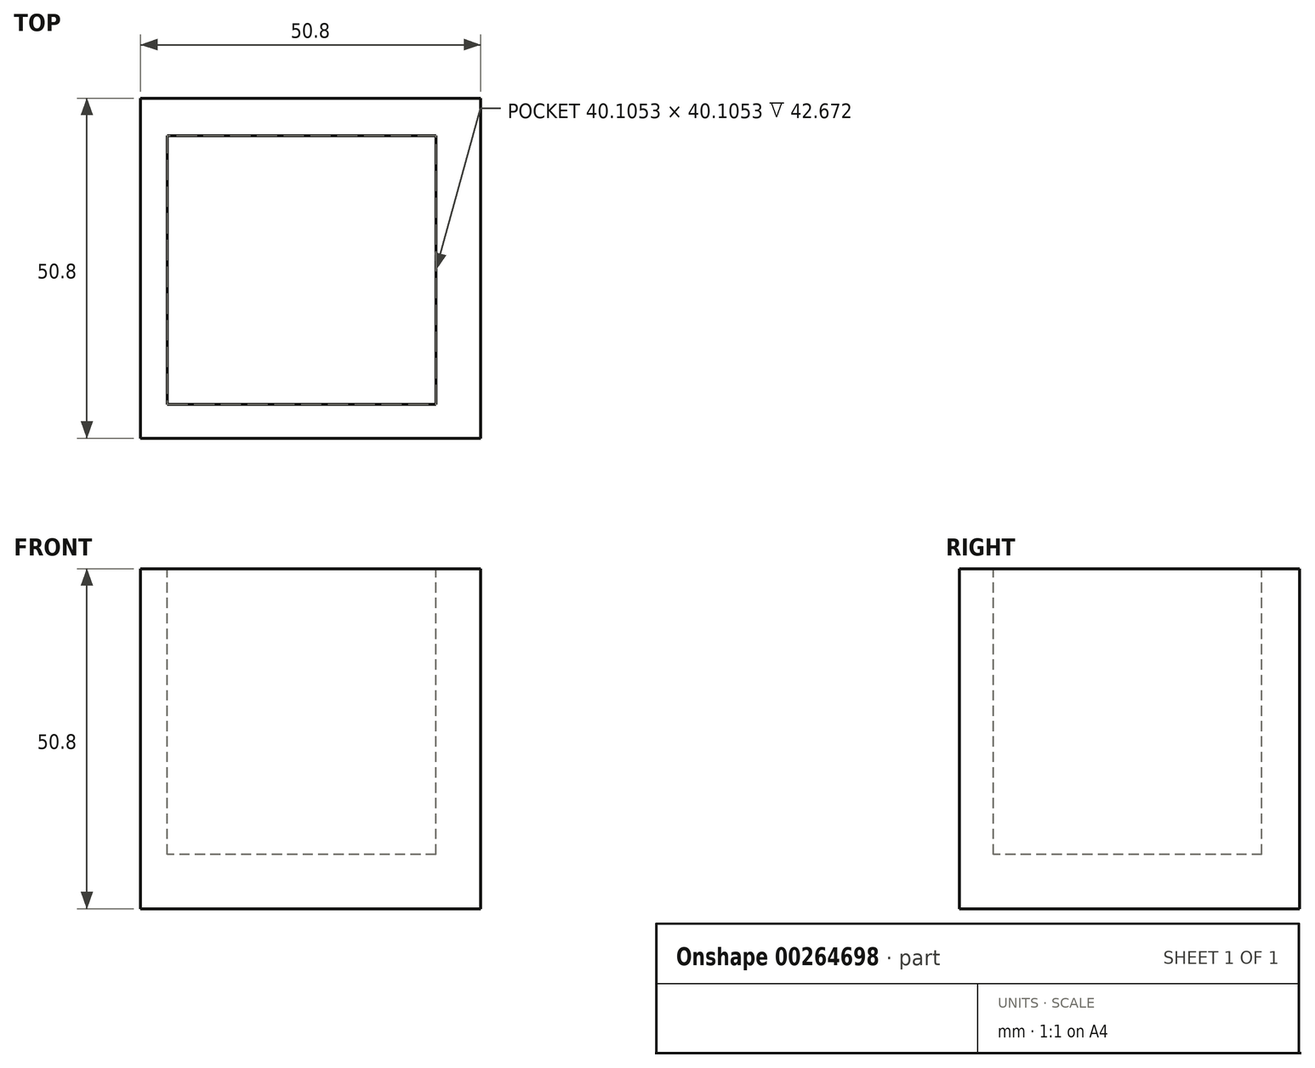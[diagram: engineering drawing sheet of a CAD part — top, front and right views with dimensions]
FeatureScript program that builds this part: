
annotation { "Feature Type Name" : "Feature", "Feature Type Description" : "" }
export const myFeature = defineFeature(function(context is Context, id is Id, definition is map)
    precondition{}
    {
        {
            var Q0;
            Q0=qCreatedBy(makeId("Front.planeOp"),FACE);
            var sketch = newSketch(context, id + "F0", { "sketchPlane" : qUnion([Q0])});
            skLineSegment(sketch, "E0.bottom", {"start": v(0, 0) * mm, "end": v(50.8, 0) * mm});
            skLineSegment(sketch, "E0.top", {"start": v(0, 50.8) * mm, "end": v(50.8, 50.8) * mm});
            skLineSegment(sketch, "E0.left", {"start": v(0, 0) * mm, "end": v(0, 50.8) * mm});
            skLineSegment(sketch, "E0.right", {"start": v(50.8, 0) * mm, "end": v(50.8, 50.8) * mm});
            skSolve(sketch);
        }
        {
            var Q0;
            Q0 = qSketchRegion(id + "F0", true);
            extrude(context, id + "F1", {"entities" : qUnion([Q0]), "depth" : 50.8 * mm});
        }
        {
            var Q0;
            Q0=makeQuery(id+"F1.opExtrude","SWEPT_FACE",FACE,{"disambiguationData":[OSD([sQuery(id+"F0.wireOp",EDGE,"E0.top")])]});
            var sketch = newSketch(context, id + "F2", { "sketchPlane" : qUnion([Q0])});
            skLineSegment(sketch, "E1.bottom", {"start": v(44.12, -5.61) * mm, "end": v(4.01, -5.61) * mm});
            skLineSegment(sketch, "E1.top", {"start": v(44.12, -45.72) * mm, "end": v(4.01, -45.72) * mm});
            skLineSegment(sketch, "E1.left", {"start": v(44.12, -5.61) * mm, "end": v(44.12, -45.72) * mm});
            skLineSegment(sketch, "E1.right", {"start": v(4.01, -5.61) * mm, "end": v(4.01, -45.72) * mm});
            skPoint(sketch, "E1.middle", {"position": v(24.06, -25.67) * mm});
            skSolve(sketch);
        }
        {
            var Q0;
            Q0 = qSketchRegion(id + "F2", true);
            extrude(context, id + "F3", {"entities" : qUnion([Q0]), "operationType" : NewBodyOperationType.REMOVE, "oppositeDirection" : true, "depth" : 42.67 * mm});
        }
    });
